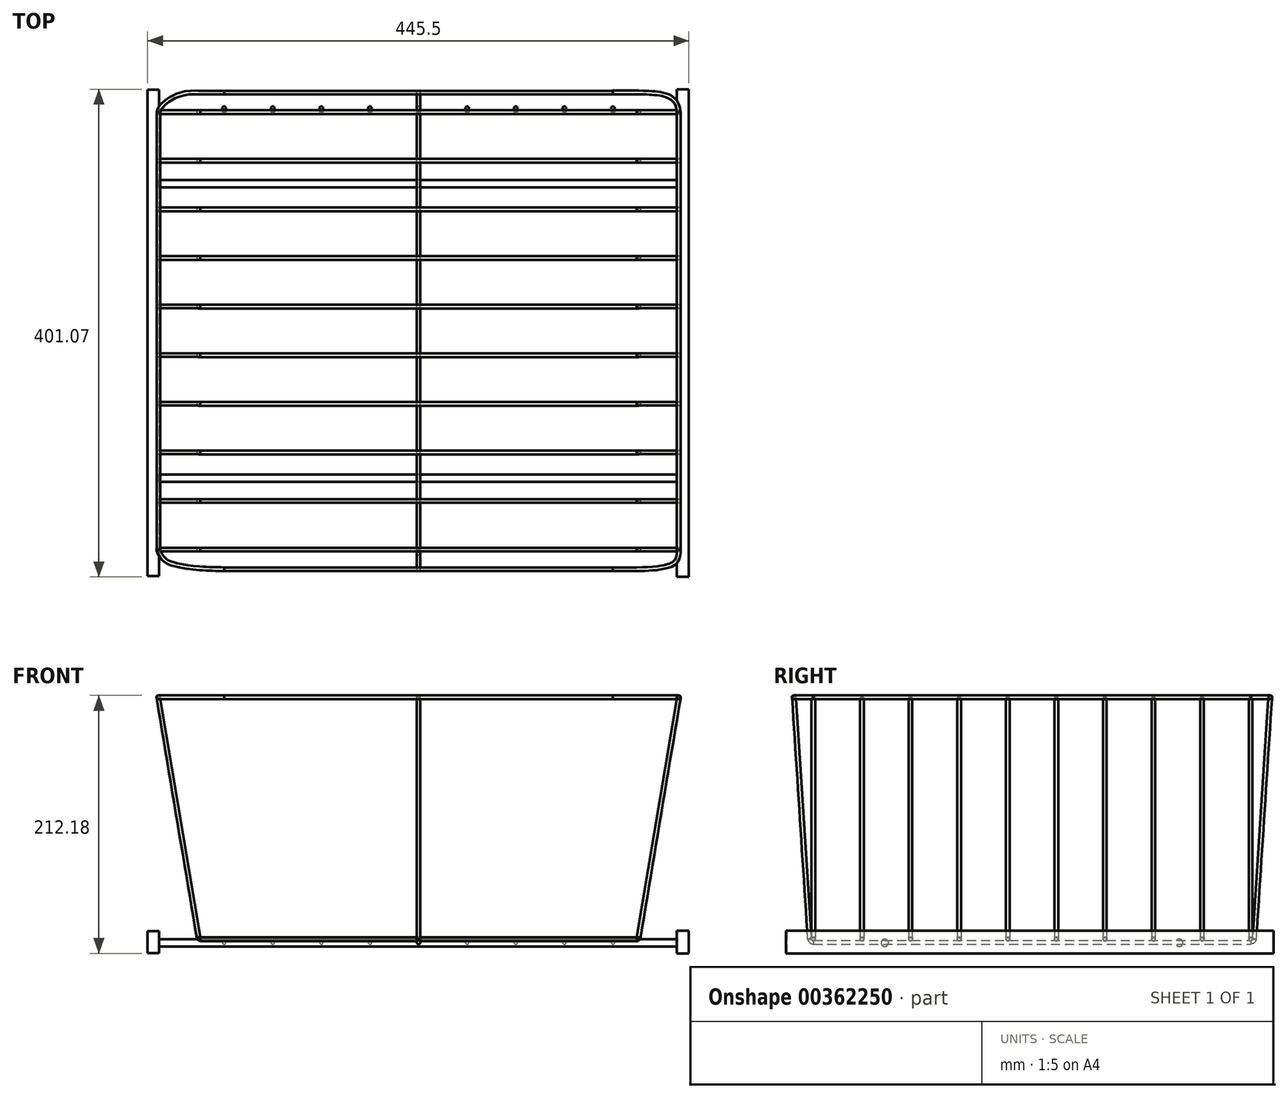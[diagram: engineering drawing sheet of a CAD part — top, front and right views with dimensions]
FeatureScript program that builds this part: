
annotation { "Feature Type Name" : "Feature", "Feature Type Description" : "" }
export const myFeature = defineFeature(function(context is Context, id is Id, definition is map)
    precondition{}
    {
        {
            var Q0;
            Q0=qCreatedBy(makeId("Front.planeOp"),FACE);
            var sketch = newSketch(context, id + "F0", { "sketchPlane" : qUnion([Q0])});
            skLineSegment(sketch, "E0.bottom", {"start": v(-179.58, 0) * mm, "end": v(180.42, 0) * mm});
            skLineSegment(sketch, "E0.top", {"start": v(-179.58, -1.5) * mm, "end": v(180.42, -1.5) * mm});
            skLineSegment(sketch, "E0.left", {"start": v(-179.58, 0) * mm, "end": v(-179.58, -1.5) * mm});
            skLineSegment(sketch, "E0.right", {"start": v(180.42, 0) * mm, "end": v(180.42, -1.5) * mm});
            skSolve(sketch);
        }
        {
            var Q0;
            Q0=makeQuery(id+"F0.imprint","IMPRINT",FACE,{"disambiguationData":[TD([[makeQuery(id+"F0.imprint","IMPRINT",EDGE,{"derivedFrom":sQuery(id+"F0.wireOp",EDGE,"E0.bottom")}),-1.0]])]});
            var Q1;
            Q1=sQuery(id+"F0.wireOp",EDGE,"E0.bottom");
            revolve(context, id + "F1", {"entities" : qUnion([Q0]), "axis" : qUnion([Q1]), "revolveType" : RevolveType.FULL});
        }
        {
            var Q0;
            Q0=qCreatedBy(makeId("Front.planeOp"),FACE);
            var sketch = newSketch(context, id + "F2", { "sketchPlane" : qUnion([Q0])});
            skLineSegment(sketch, "E1", {"start": v(-179.62, 1.46) * mm, "end": v(-212.66, 198.71) * mm});
            skLineSegment(sketch, "E2", {"start": v(-212.66, 198.71) * mm, "end": v(-214.16, 198.71) * mm});
            skLineSegment(sketch, "E3", {"start": v(-181.12, 1.46) * mm, "end": v(-179.62, 1.46) * mm});
            skLineSegment(sketch, "E4", {"start": v(-181.12, 1.46) * mm, "end": v(-214.16, 198.71) * mm});
            skSolve(sketch);
        }
        {
            var Q0;
            Q0=qSketchRegion(id+"F2",true);
            var Q1;
            Q1=sQuery(id+"F2.wireOp",EDGE,"E4");
            revolve(context, id + "F3", {"entities" : qUnion([Q0]), "axis" : qUnion([Q1]), "revolveType" : RevolveType.FULL});
        }
        {
            var Q0;
            Q0=qCreatedBy(makeId("Front.planeOp"),FACE);
            var sketch = newSketch(context, id + "F4", { "sketchPlane" : qUnion([Q0])});
            skFitSpline(sketch, "E5", {"points": [v(-182.54, 1) * mm, v(-182.18, 0.12) * mm, v(-180.93, -1.14) * mm, v(-179.6, -1.47) * mm], "startDerivative": vector(0.9, -2.93) * mm, "endDerivative": vector(4, -0.37) * mm});
            skSolve(sketch);
        }
        {
            var Q0;
            Q0=makeQuery(id+"F1.opRevolve","SWEPT_FACE",FACE,{"disambiguationData":[OSD([sQuery(id+"F0.wireOp",EDGE,"E0.left")])]});
            var Q1;
            Q1=sQuery(id+"F4.wireOp",EDGE,"E5");
            sweep(context, id + "F5", {"profiles" : qUnion([Q0]), "path" : qUnion([Q1])});
        }
        {
            var Q0;
            Q0=makeQuery(id+"F3.opRevolve","SWEPT_BODY",BODY,{"disambiguationData":[OSD([sQuery(id+"F2.wireOp",EDGE,"E1"),sQuery(id+"F2.wireOp",EDGE,"E2"),sQuery(id+"F2.wireOp",EDGE,"E3"),sQuery(id+"F2.wireOp",EDGE,"E4")])]});
            var Q1;
            Q1=makeQuery(id+"F5.opSweep","SWEPT_BODY",BODY,{"disambiguationData":[OSD([sQuery(id+"F0.wireOp",EDGE,"E0.left"),sQuery(id+"F4.wireOp",EDGE,"E5")])]});
            var Q2;
            Q2=qCreatedBy(makeId("Right.planeOp"),FACE);
            mirror(context, id + "F6", {"operationType" : NewBodyOperationType.ADD, "entities" : qUnion([Q0, Q1]), "mirrorPlane" : qUnion([Q2])});
        }
        {
            var Q0;
            Q0=makeQuery(id+"F1.opRevolve","SWEPT_BODY",BODY,{"disambiguationData":[OSD([sQuery(id+"F0.wireOp",EDGE,"E0.bottom"),sQuery(id+"F0.wireOp",EDGE,"E0.top"),sQuery(id+"F0.wireOp",EDGE,"E0.left"),sQuery(id+"F0.wireOp",EDGE,"E0.right")])]});
            transform(context, id + "F7", {"entities" : qUnion([Q0]), "transformType" : TransformType.TRANSLATION_3D, "dx" : 0 * mm, "dy" : 40 * mm, "dz" : 0 * mm, "makeCopy" : true});
        }
        {
            var Q0;
            Q0=makeQuery(id+"F7.opPattern","COPY",BODY,{"derivedFrom":makeQuery(id+"F1.opRevolve","SWEPT_BODY",BODY,{"disambiguationData":[OSD([sQuery(id+"F0.wireOp",EDGE,"E0.bottom"),sQuery(id+"F0.wireOp",EDGE,"E0.top"),sQuery(id+"F0.wireOp",EDGE,"E0.left"),sQuery(id+"F0.wireOp",EDGE,"E0.right")])]}),"instanceName":"1"});
            transform(context, id + "F8", {"entities" : qUnion([Q0]), "transformType" : TransformType.TRANSLATION_3D, "dx" : 0 * mm, "dy" : 40 * mm, "dz" : 0 * mm, "makeCopy" : true});
        }
        {
            var Q0;
            Q0=makeQuery(id+"F8.opPattern","COPY",BODY,{"derivedFrom":makeQuery(id+"F7.opPattern","COPY",BODY,{"derivedFrom":makeQuery(id+"F1.opRevolve","SWEPT_BODY",BODY,{"disambiguationData":[OSD([sQuery(id+"F0.wireOp",EDGE,"E0.bottom"),sQuery(id+"F0.wireOp",EDGE,"E0.top"),sQuery(id+"F0.wireOp",EDGE,"E0.left"),sQuery(id+"F0.wireOp",EDGE,"E0.right")])]}),"instanceName":"1"}),"instanceName":"1"});
            transform(context, id + "F9", {"entities" : qUnion([Q0]), "transformType" : TransformType.TRANSLATION_3D, "dx" : 0 * mm, "dy" : 40 * mm, "dz" : 0 * mm, "makeCopy" : true});
        }
        {
            var Q0;
            Q0=makeQuery(id+"F9.opPattern","COPY",BODY,{"derivedFrom":makeQuery(id+"F8.opPattern","COPY",BODY,{"derivedFrom":makeQuery(id+"F7.opPattern","COPY",BODY,{"derivedFrom":makeQuery(id+"F1.opRevolve","SWEPT_BODY",BODY,{"disambiguationData":[OSD([sQuery(id+"F0.wireOp",EDGE,"E0.bottom"),sQuery(id+"F0.wireOp",EDGE,"E0.top"),sQuery(id+"F0.wireOp",EDGE,"E0.left"),sQuery(id+"F0.wireOp",EDGE,"E0.right")])]}),"instanceName":"1"}),"instanceName":"1"}),"instanceName":"1"});
            transform(context, id + "F10", {"entities" : qUnion([Q0]), "transformType" : TransformType.TRANSLATION_3D, "dx" : 0 * mm, "dy" : 40 * mm, "dz" : 0 * mm, "makeCopy" : true});
        }
        {
            var Q0;
            Q0=makeQuery(id+"F10.opPattern","COPY",BODY,{"derivedFrom":makeQuery(id+"F9.opPattern","COPY",BODY,{"derivedFrom":makeQuery(id+"F8.opPattern","COPY",BODY,{"derivedFrom":makeQuery(id+"F7.opPattern","COPY",BODY,{"derivedFrom":makeQuery(id+"F1.opRevolve","SWEPT_BODY",BODY,{"disambiguationData":[OSD([sQuery(id+"F0.wireOp",EDGE,"E0.bottom"),sQuery(id+"F0.wireOp",EDGE,"E0.top"),sQuery(id+"F0.wireOp",EDGE,"E0.left"),sQuery(id+"F0.wireOp",EDGE,"E0.right")])]}),"instanceName":"1"}),"instanceName":"1"}),"instanceName":"1"}),"instanceName":"1"});
            transform(context, id + "F11", {"entities" : qUnion([Q0]), "transformType" : TransformType.TRANSLATION_3D, "dx" : 0 * mm, "dy" : 40 * mm, "dz" : 0 * mm, "makeCopy" : true});
        }
        {
            var Q0;
            Q0=makeQuery(id+"F11.opPattern","COPY",BODY,{"derivedFrom":makeQuery(id+"F10.opPattern","COPY",BODY,{"derivedFrom":makeQuery(id+"F9.opPattern","COPY",BODY,{"derivedFrom":makeQuery(id+"F8.opPattern","COPY",BODY,{"derivedFrom":makeQuery(id+"F7.opPattern","COPY",BODY,{"derivedFrom":makeQuery(id+"F1.opRevolve","SWEPT_BODY",BODY,{"disambiguationData":[OSD([sQuery(id+"F0.wireOp",EDGE,"E0.bottom"),sQuery(id+"F0.wireOp",EDGE,"E0.top"),sQuery(id+"F0.wireOp",EDGE,"E0.left"),sQuery(id+"F0.wireOp",EDGE,"E0.right")])]}),"instanceName":"1"}),"instanceName":"1"}),"instanceName":"1"}),"instanceName":"1"}),"instanceName":"1"});
            transform(context, id + "F12", {"entities" : qUnion([Q0]), "transformType" : TransformType.TRANSLATION_3D, "dx" : 0 * mm, "dy" : 40 * mm, "dz" : 0 * mm, "makeCopy" : true});
        }
        {
            var Q0;
            Q0=makeQuery(id+"F12.opPattern","COPY",BODY,{"derivedFrom":makeQuery(id+"F11.opPattern","COPY",BODY,{"derivedFrom":makeQuery(id+"F10.opPattern","COPY",BODY,{"derivedFrom":makeQuery(id+"F9.opPattern","COPY",BODY,{"derivedFrom":makeQuery(id+"F8.opPattern","COPY",BODY,{"derivedFrom":makeQuery(id+"F7.opPattern","COPY",BODY,{"derivedFrom":makeQuery(id+"F1.opRevolve","SWEPT_BODY",BODY,{"disambiguationData":[OSD([sQuery(id+"F0.wireOp",EDGE,"E0.bottom"),sQuery(id+"F0.wireOp",EDGE,"E0.top"),sQuery(id+"F0.wireOp",EDGE,"E0.left"),sQuery(id+"F0.wireOp",EDGE,"E0.right")])]}),"instanceName":"1"}),"instanceName":"1"}),"instanceName":"1"}),"instanceName":"1"}),"instanceName":"1"}),"instanceName":"1"});
            transform(context, id + "F13", {"entities" : qUnion([Q0]), "transformType" : TransformType.TRANSLATION_3D, "dx" : 0 * mm, "dy" : 40 * mm, "dz" : 0 * mm, "makeCopy" : true});
        }
        {
            var Q0;
            Q0=makeQuery(id+"F13.opPattern","COPY",BODY,{"derivedFrom":makeQuery(id+"F12.opPattern","COPY",BODY,{"derivedFrom":makeQuery(id+"F11.opPattern","COPY",BODY,{"derivedFrom":makeQuery(id+"F10.opPattern","COPY",BODY,{"derivedFrom":makeQuery(id+"F9.opPattern","COPY",BODY,{"derivedFrom":makeQuery(id+"F8.opPattern","COPY",BODY,{"derivedFrom":makeQuery(id+"F7.opPattern","COPY",BODY,{"derivedFrom":makeQuery(id+"F1.opRevolve","SWEPT_BODY",BODY,{"disambiguationData":[OSD([sQuery(id+"F0.wireOp",EDGE,"E0.bottom"),sQuery(id+"F0.wireOp",EDGE,"E0.top"),sQuery(id+"F0.wireOp",EDGE,"E0.left"),sQuery(id+"F0.wireOp",EDGE,"E0.right")])]}),"instanceName":"1"}),"instanceName":"1"}),"instanceName":"1"}),"instanceName":"1"}),"instanceName":"1"}),"instanceName":"1"}),"instanceName":"1"});
            transform(context, id + "F14", {"entities" : qUnion([Q0]), "transformType" : TransformType.TRANSLATION_3D, "dx" : 0 * mm, "dy" : 40 * mm, "dz" : 0 * mm, "makeCopy" : true});
        }
        {
            var Q0;
            Q0=makeQuery(id+"F14.opPattern","COPY",BODY,{"derivedFrom":makeQuery(id+"F13.opPattern","COPY",BODY,{"derivedFrom":makeQuery(id+"F12.opPattern","COPY",BODY,{"derivedFrom":makeQuery(id+"F11.opPattern","COPY",BODY,{"derivedFrom":makeQuery(id+"F10.opPattern","COPY",BODY,{"derivedFrom":makeQuery(id+"F9.opPattern","COPY",BODY,{"derivedFrom":makeQuery(id+"F8.opPattern","COPY",BODY,{"derivedFrom":makeQuery(id+"F7.opPattern","COPY",BODY,{"derivedFrom":makeQuery(id+"F1.opRevolve","SWEPT_BODY",BODY,{"disambiguationData":[OSD([sQuery(id+"F0.wireOp",EDGE,"E0.bottom"),sQuery(id+"F0.wireOp",EDGE,"E0.top"),sQuery(id+"F0.wireOp",EDGE,"E0.left"),sQuery(id+"F0.wireOp",EDGE,"E0.right")])]}),"instanceName":"1"}),"instanceName":"1"}),"instanceName":"1"}),"instanceName":"1"}),"instanceName":"1"}),"instanceName":"1"}),"instanceName":"1"}),"instanceName":"1"});
            transform(context, id + "F15", {"entities" : qUnion([Q0]), "transformType" : TransformType.TRANSLATION_3D, "dx" : 0 * mm, "dy" : 40 * mm, "dz" : 0 * mm, "makeCopy" : true});
        }
        {
            var Q0;
            Q0=qCreatedBy(makeId("Right.planeOp"),FACE);
            var sketch = newSketch(context, id + "F16", { "sketchPlane" : qUnion([Q0])});
            skLineSegment(sketch, "E6.bottom", {"start": v(360, -1.07) * mm, "end": v(0, -1.07) * mm});
            skLineSegment(sketch, "E6.top", {"start": v(360, -2.57) * mm, "end": v(0, -2.57) * mm});
            skLineSegment(sketch, "E6.left", {"start": v(360, -1.07) * mm, "end": v(360, -2.57) * mm});
            skLineSegment(sketch, "E6.right", {"start": v(0, -1.07) * mm, "end": v(0, -2.57) * mm});
            skSolve(sketch);
        }
        {
            var Q0;
            Q0=qSketchRegion(id+"F16",true);
            var Q1;
            Q1=sQuery(id+"F16.wireOp",EDGE,"E6.top");
            revolve(context, id + "F17", {"entities" : qUnion([Q0]), "axis" : qUnion([Q1]), "revolveType" : RevolveType.FULL});
        }
        {
            var Q0;
            Q0=qCreatedBy(makeId("Right.planeOp"),FACE);
            var sketch = newSketch(context, id + "F18", { "sketchPlane" : qUnion([Q0])});
            skLineSegment(sketch, "E7", {"start": v(-1.6, 0) * mm, "end": v(-14.52, 199.58) * mm});
            skLineSegment(sketch, "E8", {"start": v(-14.52, 199.58) * mm, "end": v(-16.02, 199.58) * mm});
            skLineSegment(sketch, "E9", {"start": v(-16.02, 199.58) * mm, "end": v(-3.1, 0) * mm});
            skLineSegment(sketch, "E10", {"start": v(-3.1, 0) * mm, "end": v(-1.6, 0) * mm});
            skSolve(sketch);
        }
        {
            var Q0;
            Q0=qSketchRegion(id+"F18",true);
            var Q1;
            Q1=sQuery(id+"F18.wireOp",EDGE,"E9");
            revolve(context, id + "F19", {"entities" : qUnion([Q0]), "axis" : qUnion([Q1]), "revolveType" : RevolveType.FULL});
        }
        {
            var Q0;
            Q0=qCreatedBy(makeId("Right.planeOp"),FACE);
            var sketch = newSketch(context, id + "F20", { "sketchPlane" : qUnion([Q0])});
            skFitSpline(sketch, "E11", {"points": [v(-4.59, -0.18) * mm, v(-3.92, -1.73) * mm, v(-1.93, -3.55) * mm, v(0, -4.03) * mm], "startDerivative": vector(1.58, -5.04) * mm, "endDerivative": vector(5.92, -0.67) * mm});
            skSolve(sketch);
        }
        {
            var Q0;
            Q0=makeQuery(id+"F17.opRevolve","SWEPT_FACE",FACE,{"disambiguationData":[OSD([sQuery(id+"F16.wireOp",EDGE,"E6.right")])]});
            var Q1;
            Q1=sQuery(id+"F20.wireOp",EDGE,"E11");
            sweep(context, id + "F21", {"profiles" : qUnion([Q0]), "path" : qUnion([Q1])});
        }
        {
            var Q0;
            Q0=qCreatedBy(makeId("Front.planeOp"),FACE);
            cPlane(context, id + "F22", {"entities" : qUnion([Q0]), "cplaneType" : CPlaneType.OFFSET, "offset" : 180 * mm, "oppositeDirection" : true, "width" : 150 * mm, "height" : 150 * mm});
        }
        {
            var Q0;
            Q0=makeQuery(id+"F19.opRevolve","SWEPT_BODY",BODY,{"disambiguationData":[OSD([sQuery(id+"F18.wireOp",EDGE,"E7"),sQuery(id+"F18.wireOp",EDGE,"E8"),sQuery(id+"F18.wireOp",EDGE,"E9"),sQuery(id+"F18.wireOp",EDGE,"E10")])]});
            var Q1;
            Q1=makeQuery(id+"F21.opSweep","SWEPT_BODY",BODY,{"disambiguationData":[OSD([sQuery(id+"F16.wireOp",EDGE,"E6.right"),sQuery(id+"F20.wireOp",EDGE,"E11")])]});
            var Q2;
            Q2=qCreatedBy(id+"F22.planeOp",FACE);
            mirror(context, id + "F23", {"entities" : qUnion([Q0, Q1]), "mirrorPlane" : qUnion([Q2])});
        }
        {
            var Q0;
            Q0=makeQuery(id+"F23.opPattern","COPY",BODY,{"derivedFrom":makeQuery(id+"F21.opSweep","SWEPT_BODY",BODY,{"disambiguationData":[OSD([sQuery(id+"F16.wireOp",EDGE,"E6.right"),sQuery(id+"F20.wireOp",EDGE,"E11")])]}),"instanceName":"1"});
            transform(context, id + "F24", {"entities" : qUnion([Q0]), "transformType" : TransformType.TRANSLATION_3D, "dx" : 40 * mm, "dy" : 0 * mm, "dz" : 0 * mm, "makeCopy" : true});
        }
        {
            var Q0;
            Q0=makeQuery(id+"F24.opPattern","COPY",BODY,{"derivedFrom":makeQuery(id+"F23.opPattern","COPY",BODY,{"derivedFrom":makeQuery(id+"F21.opSweep","SWEPT_BODY",BODY,{"disambiguationData":[OSD([sQuery(id+"F16.wireOp",EDGE,"E6.right"),sQuery(id+"F20.wireOp",EDGE,"E11")])]}),"instanceName":"1"}),"instanceName":"1"});
            transform(context, id + "F25", {"entities" : qUnion([Q0]), "transformType" : TransformType.TRANSLATION_3D, "dx" : 40 * mm, "dy" : 0 * mm, "dz" : 0 * mm, "makeCopy" : true});
        }
        {
            var Q0;
            Q0=makeQuery(id+"F25.opPattern","COPY",BODY,{"derivedFrom":makeQuery(id+"F24.opPattern","COPY",BODY,{"derivedFrom":makeQuery(id+"F23.opPattern","COPY",BODY,{"derivedFrom":makeQuery(id+"F21.opSweep","SWEPT_BODY",BODY,{"disambiguationData":[OSD([sQuery(id+"F16.wireOp",EDGE,"E6.right"),sQuery(id+"F20.wireOp",EDGE,"E11")])]}),"instanceName":"1"}),"instanceName":"1"}),"instanceName":"1"});
            transform(context, id + "F26", {"entities" : qUnion([Q0]), "transformType" : TransformType.TRANSLATION_3D, "dx" : 40 * mm, "dy" : 0 * mm, "dz" : 0 * mm, "makeCopy" : true});
        }
        {
            var Q0;
            Q0=makeQuery(id+"F26.opPattern","COPY",BODY,{"derivedFrom":makeQuery(id+"F25.opPattern","COPY",BODY,{"derivedFrom":makeQuery(id+"F24.opPattern","COPY",BODY,{"derivedFrom":makeQuery(id+"F23.opPattern","COPY",BODY,{"derivedFrom":makeQuery(id+"F21.opSweep","SWEPT_BODY",BODY,{"disambiguationData":[OSD([sQuery(id+"F16.wireOp",EDGE,"E6.right"),sQuery(id+"F20.wireOp",EDGE,"E11")])]}),"instanceName":"1"}),"instanceName":"1"}),"instanceName":"1"}),"instanceName":"1"});
            transform(context, id + "F27", {"entities" : qUnion([Q0]), "transformType" : TransformType.TRANSLATION_3D, "dx" : 40 * mm, "dy" : 0 * mm, "dz" : 0 * mm, "makeCopy" : true});
        }
        {
            var Q0;
            Q0=makeQuery(id+"F23.opPattern","COPY",BODY,{"derivedFrom":makeQuery(id+"F21.opSweep","SWEPT_BODY",BODY,{"disambiguationData":[OSD([sQuery(id+"F16.wireOp",EDGE,"E6.right"),sQuery(id+"F20.wireOp",EDGE,"E11")])]}),"instanceName":"1"});
            transform(context, id + "F28", {"entities" : qUnion([Q0]), "transformType" : TransformType.TRANSLATION_3D, "dx" : -40 * mm, "dy" : 0 * mm, "dz" : 0 * mm, "makeCopy" : true});
        }
        {
            var Q0;
            Q0=makeQuery(id+"F28.opPattern","COPY",BODY,{"derivedFrom":makeQuery(id+"F23.opPattern","COPY",BODY,{"derivedFrom":makeQuery(id+"F21.opSweep","SWEPT_BODY",BODY,{"disambiguationData":[OSD([sQuery(id+"F16.wireOp",EDGE,"E6.right"),sQuery(id+"F20.wireOp",EDGE,"E11")])]}),"instanceName":"1"}),"instanceName":"1"});
            transform(context, id + "F29", {"entities" : qUnion([Q0]), "transformType" : TransformType.TRANSLATION_3D, "dx" : -40 * mm, "dy" : 0 * mm, "dz" : 0 * mm, "makeCopy" : true});
        }
        {
            var Q0;
            Q0=makeQuery(id+"F29.opPattern","COPY",BODY,{"derivedFrom":makeQuery(id+"F28.opPattern","COPY",BODY,{"derivedFrom":makeQuery(id+"F23.opPattern","COPY",BODY,{"derivedFrom":makeQuery(id+"F21.opSweep","SWEPT_BODY",BODY,{"disambiguationData":[OSD([sQuery(id+"F16.wireOp",EDGE,"E6.right"),sQuery(id+"F20.wireOp",EDGE,"E11")])]}),"instanceName":"1"}),"instanceName":"1"}),"instanceName":"1"});
            transform(context, id + "F30", {"entities" : qUnion([Q0]), "transformType" : TransformType.TRANSLATION_3D, "dx" : -40 * mm, "dy" : 0 * mm, "dz" : 0 * mm, "makeCopy" : true});
        }
        {
            var Q0;
            Q0=makeQuery(id+"F30.opPattern","COPY",BODY,{"derivedFrom":makeQuery(id+"F29.opPattern","COPY",BODY,{"derivedFrom":makeQuery(id+"F28.opPattern","COPY",BODY,{"derivedFrom":makeQuery(id+"F23.opPattern","COPY",BODY,{"derivedFrom":makeQuery(id+"F21.opSweep","SWEPT_BODY",BODY,{"disambiguationData":[OSD([sQuery(id+"F16.wireOp",EDGE,"E6.right"),sQuery(id+"F20.wireOp",EDGE,"E11")])]}),"instanceName":"1"}),"instanceName":"1"}),"instanceName":"1"}),"instanceName":"1"});
            transform(context, id + "F31", {"entities" : qUnion([Q0]), "transformType" : TransformType.TRANSLATION_3D, "dx" : -40 * mm, "dy" : 0 * mm, "dz" : 0 * mm, "makeCopy" : true});
        }
        {
            var Q0;
            Q0=qCreatedBy(makeId("Top.planeOp"),FACE);
            cPlane(context, id + "F32", {"entities" : qUnion([Q0]), "cplaneType" : CPlaneType.OFFSET, "offset" : 199 * mm, "width" : 150 * mm, "height" : 150 * mm});
        }
        {
            var Q0;
            Q0=qCreatedBy(id+"F32.planeOp",FACE);
            var sketch = newSketch(context, id + "F33", { "sketchPlane" : qUnion([Q0])});
            skLineSegment(sketch, "E12.bottom", {"start": v(-160.03, -16.04) * mm, "end": v(159.97, -16.04) * mm});
            skLineSegment(sketch, "E12.top", {"start": v(-160.03, -17.54) * mm, "end": v(159.97, -17.54) * mm});
            skLineSegment(sketch, "E12.left", {"start": v(-160.03, -16.04) * mm, "end": v(-160.03, -17.54) * mm});
            skLineSegment(sketch, "E12.right", {"start": v(159.97, -16.04) * mm, "end": v(159.97, -17.54) * mm});
            skSolve(sketch);
        }
        {
            var Q0;
            Q0=makeQuery(id+"F33.imprint","IMPRINT",FACE,{"disambiguationData":[TD([[makeQuery(id+"F33.imprint","IMPRINT",EDGE,{"derivedFrom":sQuery(id+"F33.wireOp",EDGE,"E12.bottom")}),-1.0]])]});
            var Q1;
            Q1=sQuery(id+"F33.wireOp",EDGE,"E12.bottom");
            revolve(context, id + "F34", {"entities" : qUnion([Q0]), "axis" : qUnion([Q1]), "revolveType" : RevolveType.FULL});
        }
        {
            var Q0;
            Q0=qCreatedBy(id+"F32.planeOp",FACE);
            var sketch = newSketch(context, id + "F35", { "sketchPlane" : qUnion([Q0])});
            skLineSegment(sketch, "E13.bottom", {"start": v(-160.06, 376.04) * mm, "end": v(159.94, 376.04) * mm});
            skLineSegment(sketch, "E13.top", {"start": v(-160.06, 377.54) * mm, "end": v(159.94, 377.54) * mm});
            skLineSegment(sketch, "E13.left", {"start": v(-160.06, 376.04) * mm, "end": v(-160.06, 377.54) * mm});
            skLineSegment(sketch, "E13.right", {"start": v(159.94, 376.04) * mm, "end": v(159.94, 377.54) * mm});
            skSolve(sketch);
        }
        {
            var Q0;
            Q0=qSketchRegion(id+"F35",true);
            var Q1;
            Q1=sQuery(id+"F35.wireOp",EDGE,"E13.bottom");
            revolve(context, id + "F36", {"entities" : qUnion([Q0]), "axis" : qUnion([Q1]), "revolveType" : RevolveType.FULL});
        }
        {
            var Q0;
            Q0=qCreatedBy(id+"F32.planeOp",FACE);
            var sketch = newSketch(context, id + "F37", { "sketchPlane" : qUnion([Q0])});
            skLineSegment(sketch, "E14.bottom", {"start": v(-215.6, 360) * mm, "end": v(-214.1, 360) * mm});
            skLineSegment(sketch, "E14.top", {"start": v(-215.6, 0) * mm, "end": v(-214.1, 0) * mm});
            skLineSegment(sketch, "E14.left", {"start": v(-215.6, 360) * mm, "end": v(-215.6, 0) * mm});
            skLineSegment(sketch, "E14.right", {"start": v(-214.1, 360) * mm, "end": v(-214.1, 0) * mm});
            skSolve(sketch);
        }
        {
            var Q0;
            Q0=qSketchRegion(id+"F37",true);
            var Q1;
            Q1=sQuery(id+"F37.wireOp",EDGE,"E14.right");
            revolve(context, id + "F38", {"entities" : qUnion([Q0]), "axis" : qUnion([Q1]), "revolveType" : RevolveType.FULL});
        }
        {
            var Q0;
            Q0=qCreatedBy(id+"F32.planeOp",FACE);
            var sketch = newSketch(context, id + "F39", { "sketchPlane" : qUnion([Q0])});
            skFitSpline(sketch, "E15", {"points": [v(-215.61, 0) * mm, v(-201.65, -13.22) * mm, v(-185.72, -16.08) * mm, v(-159.95, -17.32) * mm], "startDerivative": vector(28.9, -88.62) * mm, "endDerivative": vector(69.27, -0.56) * mm});
            skSolve(sketch);
        }
        {
            var Q0;
            Q0=makeQuery(id+"F34.opRevolve","SWEPT_FACE",FACE,{"disambiguationData":[OSD([sQuery(id+"F33.wireOp",EDGE,"E12.left")])]});
            var Q1;
            Q1=sQuery(id+"F39.wireOp",EDGE,"E15");
            sweep(context, id + "F40", {"profiles" : qUnion([Q0]), "path" : qUnion([Q1])});
        }
        {
            var Q0;
            Q0=qCreatedBy(id+"F32.planeOp",FACE);
            var sketch = newSketch(context, id + "F41", { "sketchPlane" : qUnion([Q0])});
            skFitSpline(sketch, "E16", {"points": [v(-160.14, 377.49) * mm, v(-177.98, 377.45) * mm, v(-198.2, 375.36) * mm, v(-215.39, 360.13) * mm], "startDerivative": vector(-59.47, -0.43) * mm, "endDerivative": vector(-3.54, -51.4) * mm});
            skSolve(sketch);
        }
        {
            var Q0;
            Q0=makeQuery(id+"F36.opRevolve","SWEPT_FACE",FACE,{"disambiguationData":[OSD([sQuery(id+"F35.wireOp",EDGE,"E13.left")])]});
            var Q1;
            Q1=sQuery(id+"F41.wireOp",EDGE,"E16");
            sweep(context, id + "F42", {"profiles" : qUnion([Q0]), "path" : qUnion([Q1])});
        }
        {
            var Q0;
            Q0=qCreatedBy(id+"F32.planeOp",FACE);
            var sketch = newSketch(context, id + "F43", { "sketchPlane" : qUnion([Q0])});
            skLineSegment(sketch, "E17.bottom", {"start": v(214.08, 360) * mm, "end": v(215.58, 360) * mm});
            skLineSegment(sketch, "E17.top", {"start": v(214.08, 0) * mm, "end": v(215.58, 0) * mm});
            skLineSegment(sketch, "E17.left", {"start": v(214.08, 360) * mm, "end": v(214.08, 0) * mm});
            skLineSegment(sketch, "E17.right", {"start": v(215.58, 360) * mm, "end": v(215.58, 0) * mm});
            skSolve(sketch);
        }
        {
            var Q0;
            Q0=qSketchRegion(id+"F43",true);
            var Q1;
            Q1=sQuery(id+"F43.wireOp",EDGE,"E17.left");
            revolve(context, id + "F44", {"entities" : qUnion([Q0]), "axis" : qUnion([Q1]), "revolveType" : RevolveType.FULL});
        }
        {
            var Q0;
            Q0=qCreatedBy(id+"F32.planeOp",FACE);
            var sketch = newSketch(context, id + "F45", { "sketchPlane" : qUnion([Q0])});
            skFitSpline(sketch, "E18", {"points": [v(159.86, -17.3) * mm, v(193.94, -16.7) * mm, v(210.75, -12.31) * mm, v(215.54, 0) * mm], "startDerivative": vector(59.2, -0.2) * mm, "endDerivative": vector(3.02, 82.73) * mm});
            skSolve(sketch);
        }
        {
            var Q0;
            Q0=makeQuery(id+"F34.opRevolve","SWEPT_FACE",FACE,{"disambiguationData":[OSD([sQuery(id+"F33.wireOp",EDGE,"E12.right")])]});
            var Q1;
            Q1=sQuery(id+"F45.wireOp",EDGE,"E18");
            sweep(context, id + "F46", {"profiles" : qUnion([Q0]), "path" : qUnion([Q1])});
        }
        {
            var Q0;
            Q0=qCreatedBy(id+"F32.planeOp",FACE);
            var sketch = newSketch(context, id + "F47", { "sketchPlane" : qUnion([Q0])});
            skFitSpline(sketch, "E19", {"points": [v(159.76, 377.64) * mm, v(188.68, 377.38) * mm, v(206.7, 374.17) * mm, v(215.56, 360.06) * mm], "startDerivative": vector(107.52, 0.78) * mm, "endDerivative": vector(1.64, -73.97) * mm});
            skSolve(sketch);
        }
        {
            var Q0;
            Q0=makeQuery(id+"F44.opRevolve","SWEPT_FACE",FACE,{"disambiguationData":[OSD([sQuery(id+"F43.wireOp",EDGE,"E17.bottom")])]});
            var Q1;
            Q1=sQuery(id+"F47.wireOp",EDGE,"E19");
            sweep(context, id + "F48", {"profiles" : qUnion([Q0]), "path" : qUnion([Q1])});
        }
        {
            var Q0;
            Q0=qCreatedBy(makeId("Top.planeOp"),FACE);
            cPlane(context, id + "F49", {"entities" : qUnion([Q0]), "cplaneType" : CPlaneType.OFFSET, "offset" : 3 * mm, "oppositeDirection" : true, "width" : 150 * mm, "height" : 150 * mm});
        }
        {
            var Q0;
            Q0=qCreatedBy(id+"F49.planeOp",FACE);
            var sketch = newSketch(context, id + "F50", { "sketchPlane" : qUnion([Q0])});
            skLineSegment(sketch, "E20.bottom", {"start": v(-213.5, 55.81) * mm, "end": v(212.5, 55.81) * mm});
            skLineSegment(sketch, "E20.top", {"start": v(-213.5, 58.81) * mm, "end": v(212.5, 58.81) * mm});
            skLineSegment(sketch, "E20.left", {"start": v(-213.5, 55.81) * mm, "end": v(-213.5, 58.81) * mm});
            skLineSegment(sketch, "E20.right", {"start": v(212.5, 55.81) * mm, "end": v(212.5, 58.81) * mm});
            skSolve(sketch);
        }
        {
            var Q0;
            Q0=qSketchRegion(id+"F50",true);
            var Q1;
            Q1=sQuery(id+"F50.wireOp",EDGE,"E20.top");
            revolve(context, id + "F51", {"entities" : qUnion([Q0]), "axis" : qUnion([Q1]), "revolveType" : RevolveType.FULL});
        }
        {
            var Q0;
            Q0=makeQuery(id+"F51.opRevolve","SWEPT_BODY",BODY,{"disambiguationData":[OSD([sQuery(id+"F50.wireOp",EDGE,"E20.bottom"),sQuery(id+"F50.wireOp",EDGE,"E20.top"),sQuery(id+"F50.wireOp",EDGE,"E20.left"),sQuery(id+"F50.wireOp",EDGE,"E20.right")])]});
            var Q1;
            Q1=qCreatedBy(id+"F22.planeOp",FACE);
            mirror(context, id + "F52", {"entities" : qUnion([Q0]), "mirrorPlane" : qUnion([Q1])});
        }
        {
            var Q0;
            Q0=makeQuery(id+"F52.opPattern","COPY",FACE,{"derivedFrom":makeQuery(id+"F51.opRevolve","SWEPT_FACE",FACE,{"disambiguationData":[OSD([sQuery(id+"F50.wireOp",EDGE,"E20.left")])]}),"instanceName":"1"});
            cPlane(context, id + "F53", {"entities" : qUnion([Q0]), "cplaneType" : CPlaneType.OFFSET, "offset" : 0 * mm, "width" : 150 * mm, "height" : 150 * mm});
        }
        {
            var Q0;
            Q0=qCreatedBy(id+"F53.planeOp",FACE);
            var sketch = newSketch(context, id + "F54", { "sketchPlane" : qUnion([Q0])});
            skLineSegment(sketch, "E21.bottom", {"start": v(-378.24, 6.58) * mm, "end": v(21.76, 6.58) * mm});
            skLineSegment(sketch, "E21.top", {"start": v(-378.24, -11.42) * mm, "end": v(21.76, -11.42) * mm});
            skLineSegment(sketch, "E21.left", {"start": v(-378.24, 6.58) * mm, "end": v(-378.24, -11.42) * mm});
            skLineSegment(sketch, "E21.right", {"start": v(21.76, 6.58) * mm, "end": v(21.76, -11.42) * mm});
            skSolve(sketch);
        }
        {
            var Q0;
            Q0=qSketchRegion(id+"F54",true);
            extrude(context, id + "F55", {"entities" : qUnion([Q0]), "depth" : 9.5 * mm});
        }
        {
            var Q0;
            Q0=makeQuery(id+"F51.opRevolve","SWEPT_FACE",FACE,{"disambiguationData":[OSD([sQuery(id+"F50.wireOp",EDGE,"E20.right")])]});
            var sketch = newSketch(context, id + "F56", { "sketchPlane" : qUnion([Q0])});
            skLineSegment(sketch, "E22.bottom", {"start": v(-22.38, 6.84) * mm, "end": v(378.69, 6.84) * mm});
            skLineSegment(sketch, "E22.top", {"start": v(-22.38, -11.68) * mm, "end": v(378.69, -11.68) * mm});
            skLineSegment(sketch, "E22.left", {"start": v(-22.38, 6.84) * mm, "end": v(-22.38, -11.68) * mm});
            skLineSegment(sketch, "E22.right", {"start": v(378.69, 6.84) * mm, "end": v(378.69, -11.68) * mm});
            skSolve(sketch);
        }
        {
            var Q0;
            Q0 = qSketchRegion(id + "F56", true);
            extrude(context, id + "F57", {"entities" : qUnion([Q0]), "operationType" : NewBodyOperationType.ADD, "depth" : 10 * mm});
        }
    });
